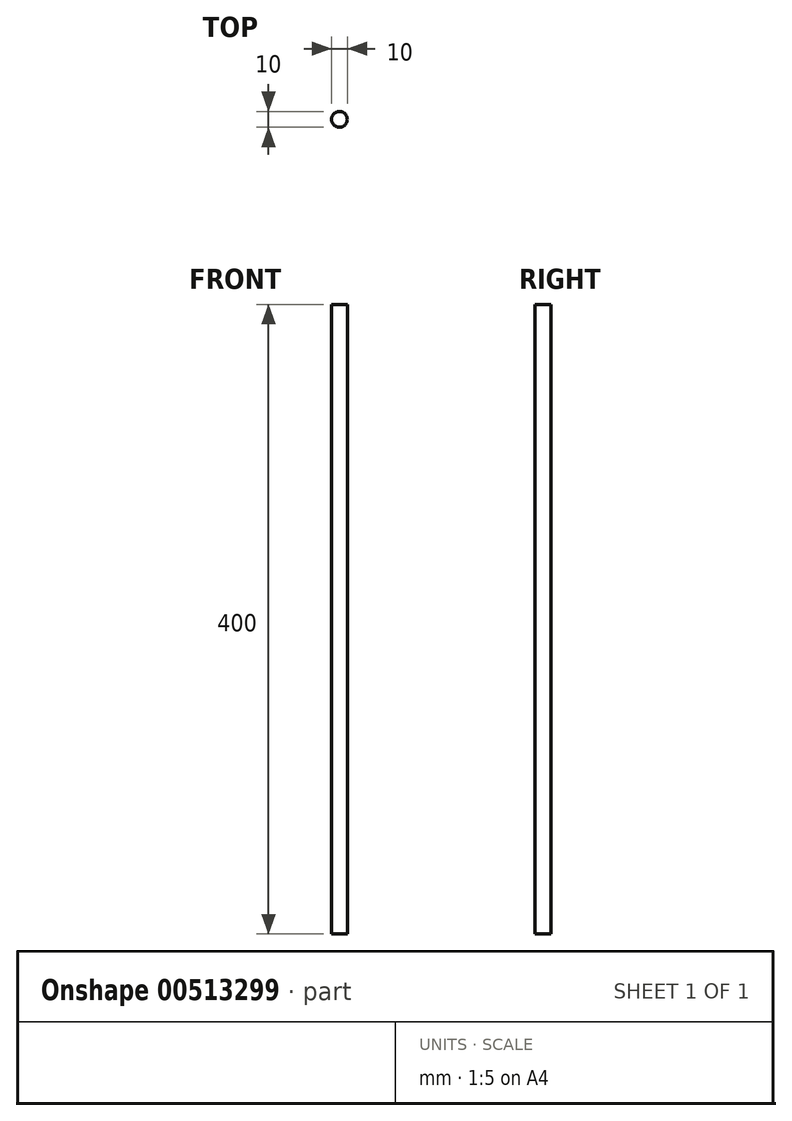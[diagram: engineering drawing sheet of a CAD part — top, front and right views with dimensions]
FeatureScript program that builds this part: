
annotation { "Feature Type Name" : "Feature", "Feature Type Description" : "" }
export const myFeature = defineFeature(function(context is Context, id is Id, definition is map)
    precondition{}
    {
        {
            var Q0;
            Q0=qCreatedBy(makeId("Top.planeOp"),FACE);
            var sketch = newSketch(context, id + "F0", { "sketchPlane" : qUnion([Q0])});
            skCircle(sketch, "E0", {"center": v(0, 0) * mm, "radius": 5 * mm});
            skSolve(sketch);
        }
        {
            var Q0;
            Q0 = qSketchRegion(id + "F0", true);
            extrude(context, id + "F1", {"entities" : qUnion([Q0]), "depth" : 400 * mm, "offsetDistance" : 25 * mm});
        }
    });
